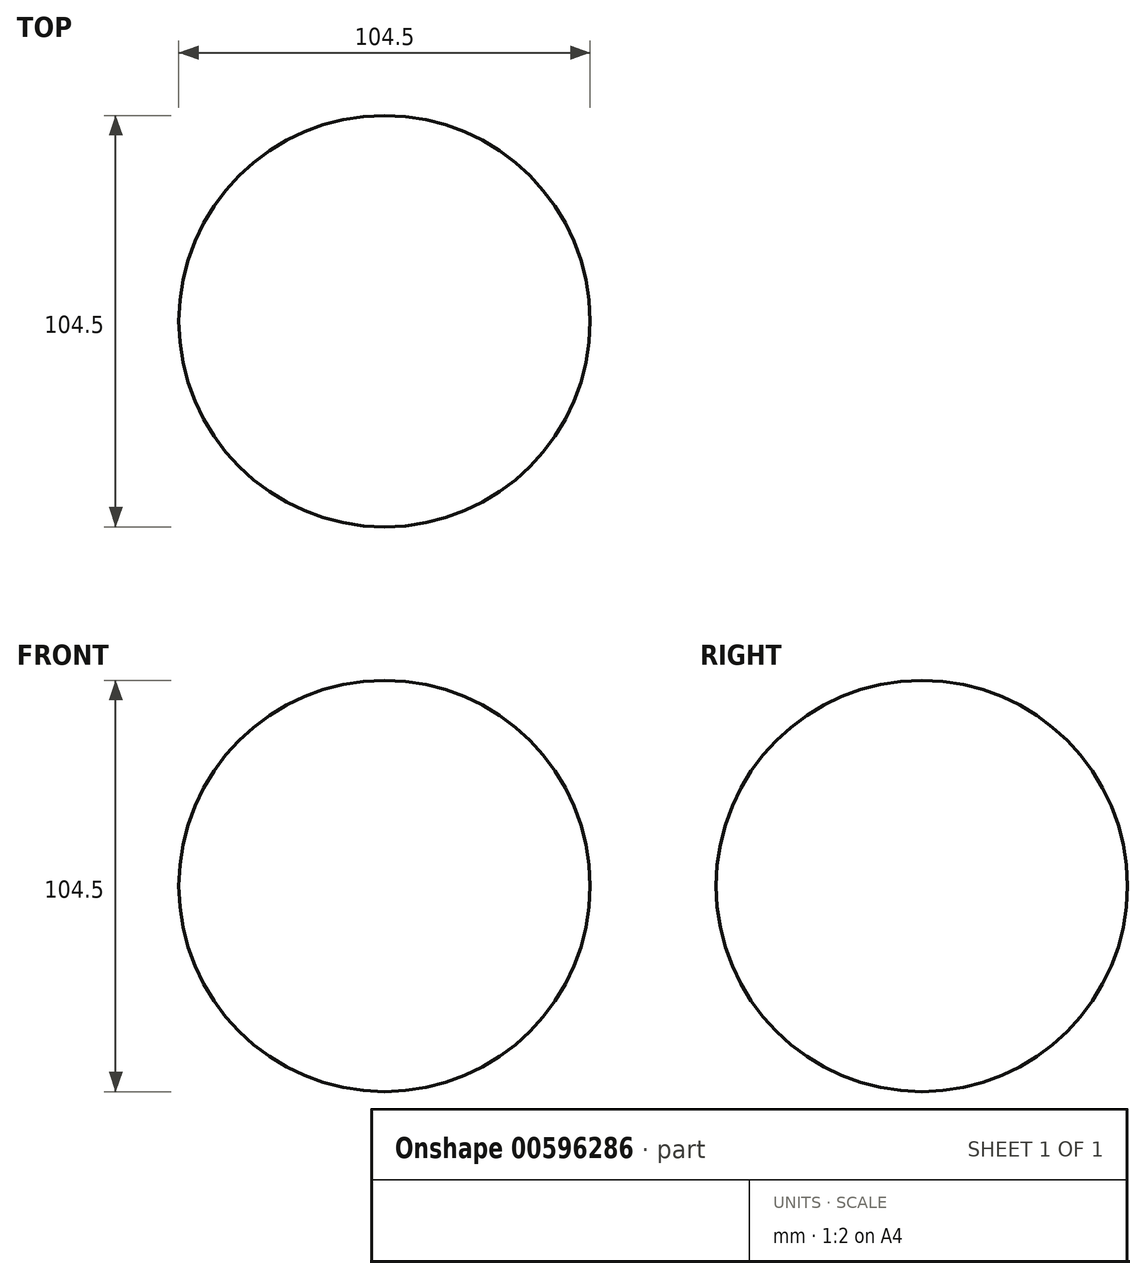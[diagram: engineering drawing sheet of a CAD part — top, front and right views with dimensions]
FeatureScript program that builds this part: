
annotation { "Feature Type Name" : "Feature", "Feature Type Description" : "" }
export const myFeature = defineFeature(function(context is Context, id is Id, definition is map)
    precondition{}
    {
        {
            var Q0;
            Q0=qCreatedBy(makeId("Front.planeOp"),FACE);
            var sketch = newSketch(context, id + "F0", { "sketchPlane" : qUnion([Q0])});
            skArc(sketch, "E0", {"start": v(0, -52.25) * mm, "mid": v(52.25, 0) * mm, "end": v(0, 52.25) * mm});
            skLineSegment(sketch, "E1", {"start": v(0, 52.25) * mm, "end": v(0, -52.25) * mm});
            skSolve(sketch);
        }
        {
            var Q0;
            Q0 = qSketchRegion(id + "F0", true);
            var Q1;
            Q1=sQuery(id+"F0.wireOp",EDGE,"E1");
            revolve(context, id + "F1", {"entities" : qUnion([Q0]), "axis" : qUnion([Q1]), "revolveType" : RevolveType.FULL});
        }
    });
